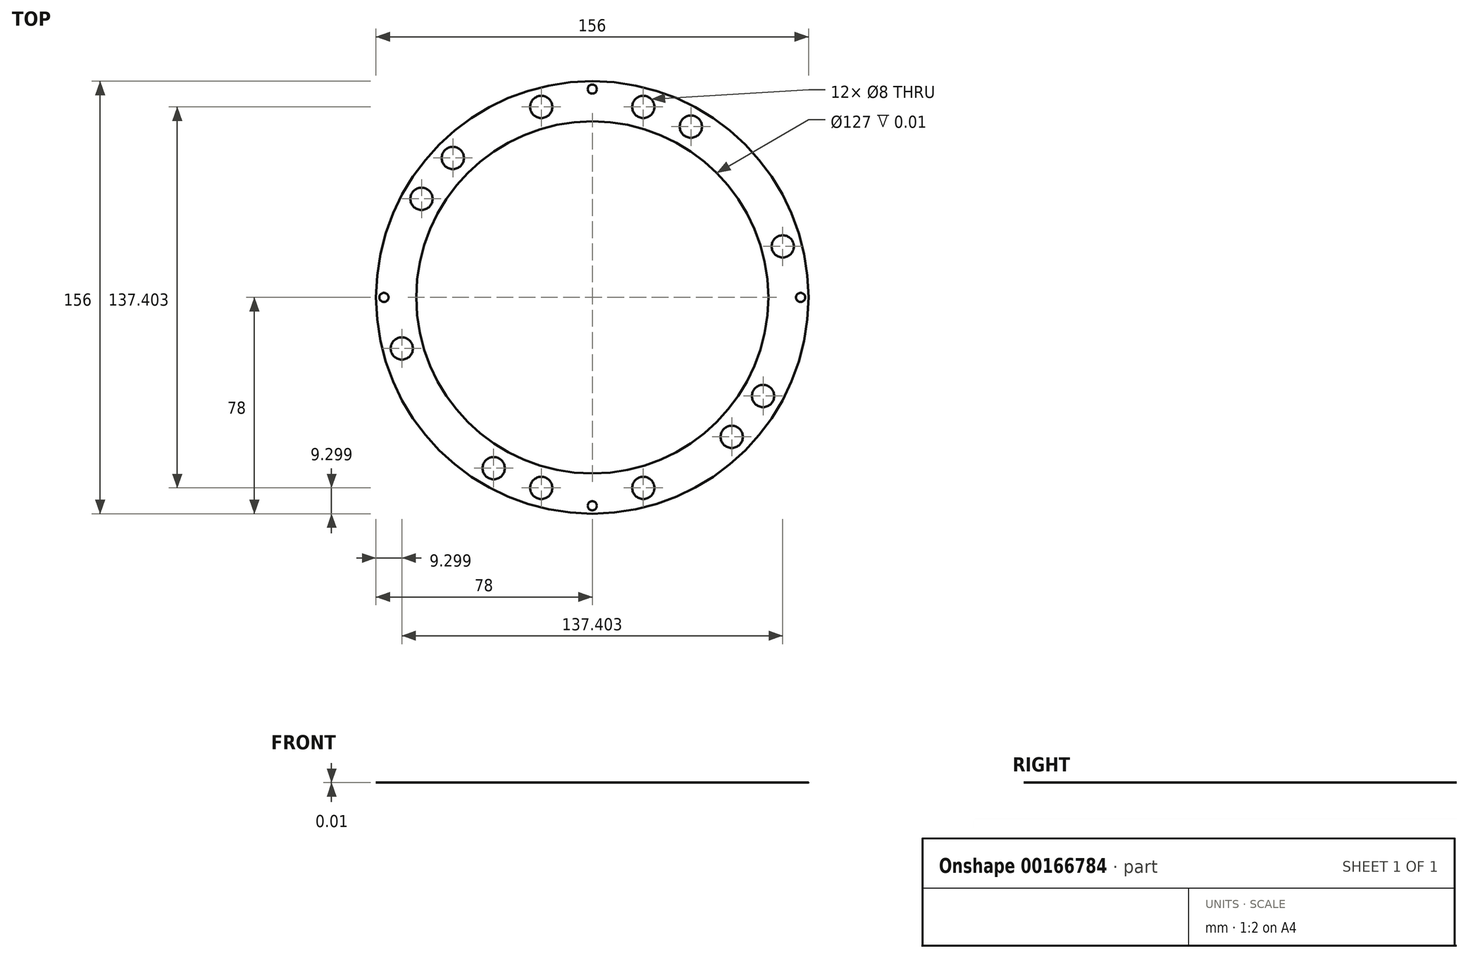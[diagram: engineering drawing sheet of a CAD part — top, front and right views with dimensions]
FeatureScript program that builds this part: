
annotation { "Feature Type Name" : "Feature", "Feature Type Description" : "" }
export const myFeature = defineFeature(function(context is Context, id is Id, definition is map)
    precondition{}
    {
        {
            var Q0;
            Q0=qCreatedBy(makeId("Top.planeOp"),FACE);
            var sketch = newSketch(context, id + "F0", { "sketchPlane" : qUnion([Q0])});
            skCircle(sketch, "E0", {"center": v(0, 0) * mm, "radius": 63.5 * mm});
            skCircle(sketch, "E1", {"center": v(0, 0) * mm, "radius": 78 * mm});
            skCircle(sketch, "E2", {"center": v(75.15, 0) * mm, "radius": 1.65 * mm});
            skCircle(sketch, "E3.1.0", {"center": v(0, 75.15) * mm, "radius": 1.65 * mm});
            skCircle(sketch, "E3.2.0", {"center": v(-75.15, 0) * mm, "radius": 1.65 * mm});
            skCircle(sketch, "E3.3.0", {"center": v(0, -75.15) * mm, "radius": 1.65 * mm});
            skCircle(sketch, "E4", {"center": v(68.7, 18.4) * mm, "radius": 2.38 * mm});
            skCircle(sketch, "E5", {"center": v(35.56, 61.6) * mm, "radius": 2.38 * mm});
            skCircle(sketch, "E6", {"center": v(18.4, 68.7) * mm, "radius": 2.38 * mm});
            skLineSegment(sketch, "E7", {"start": v(68.7, 18.4) * mm, "end": v(0, 0) * mm, "construction": true});
            skLineSegment(sketch, "E8", {"start": v(35.56, 61.6) * mm, "end": v(0, 0) * mm, "construction": true});
            skLineSegment(sketch, "E9", {"start": v(18.4, 68.7) * mm, "end": v(0, 0) * mm, "construction": true});
            skCircle(sketch, "E10.1.0", {"center": v(-18.4, -68.7) * mm, "radius": 2.38 * mm});
            skCircle(sketch, "E10.1.1", {"center": v(-68.7, -18.4) * mm, "radius": 2.38 * mm});
            skCircle(sketch, "E10.1.2", {"center": v(-35.56, -61.6) * mm, "radius": 2.38 * mm});
            skCircle(sketch, "E11", {"center": v(-18.4, 68.7) * mm, "radius": 2.38 * mm});
            skCircle(sketch, "E12", {"center": v(-50.3, 50.3) * mm, "radius": 2.38 * mm});
            skCircle(sketch, "E13", {"center": v(-61.6, 35.56) * mm, "radius": 2.38 * mm});
            skLineSegment(sketch, "E14", {"start": v(0, 0) * mm, "end": v(-18.4, 68.7) * mm, "construction": true});
            skLineSegment(sketch, "E15", {"start": v(0, 0) * mm, "end": v(-50.3, 50.3) * mm, "construction": true});
            skLineSegment(sketch, "E16", {"start": v(0, 0) * mm, "end": v(-61.6, 35.56) * mm, "construction": true});
            skCircle(sketch, "E17.1.0", {"center": v(50.3, -50.3) * mm, "radius": 2.38 * mm});
            skCircle(sketch, "E17.1.1", {"center": v(18.4, -68.7) * mm, "radius": 2.38 * mm});
            skCircle(sketch, "E17.1.2", {"center": v(61.6, -35.56) * mm, "radius": 2.38 * mm});
            skSolve(sketch);
        }
        {
            var Q0;
            Q0=makeQuery(id+"F0.imprint","IMPRINT",FACE,{"disambiguationData":[TD([[makeQuery(id+"F0.imprint","IMPRINT",EDGE,{"derivedFrom":sQuery(id+"F0.wireOp",EDGE,"E0")}),-1.0]])]});
            extrude(context, id + "F1", {"entities" : qUnion([Q0]), "depth" : 1 / 101.6 * mm});
        }
        {
            var Q0;
            Q0=makeQuery(id+"F1.opExtrude","CAP_FACE",FACE,{"disambiguationData":[OSD([sQuery(id+"F0.wireOp",EDGE,"E0"),sQuery(id+"F0.wireOp",EDGE,"E1"),sQuery(id+"F0.wireOp",EDGE,"E2"),sQuery(id+"F0.wireOp",EDGE,"E3.1.0"),sQuery(id+"F0.wireOp",EDGE,"E3.2.0"),sQuery(id+"F0.wireOp",EDGE,"E3.3.0"),sQuery(id+"F0.wireOp",EDGE,"E4"),sQuery(id+"F0.wireOp",EDGE,"E5"),sQuery(id+"F0.wireOp",EDGE,"E6"),sQuery(id+"F0.wireOp",EDGE,"E10.1.0"),sQuery(id+"F0.wireOp",EDGE,"E10.1.1"),sQuery(id+"F0.wireOp",EDGE,"E10.1.2"),sQuery(id+"F0.wireOp",EDGE,"E11"),sQuery(id+"F0.wireOp",EDGE,"E12"),sQuery(id+"F0.wireOp",EDGE,"E13"),sQuery(id+"F0.wireOp",EDGE,"E17.1.0"),sQuery(id+"F0.wireOp",EDGE,"E17.1.1"),sQuery(id+"F0.wireOp",EDGE,"E17.1.2")])],"isStart":false});
            var sketch = newSketch(context, id + "F2", { "sketchPlane" : qUnion([Q0])});
            skCircle(sketch, "E18", {"center": v(68.7, 18.4) * mm, "radius": 4 * mm});
            skCircle(sketch, "E19", {"center": v(35.56, 61.6) * mm, "radius": 4 * mm});
            skCircle(sketch, "E20", {"center": v(18.4, 68.7) * mm, "radius": 4 * mm});
            skCircle(sketch, "E21", {"center": v(-18.4, 68.7) * mm, "radius": 4 * mm});
            skCircle(sketch, "E22", {"center": v(-50.3, 50.3) * mm, "radius": 4 * mm});
            skCircle(sketch, "E23", {"center": v(-61.6, 35.56) * mm, "radius": 4 * mm});
            skCircle(sketch, "E24", {"center": v(-68.7, -18.4) * mm, "radius": 4 * mm});
            skCircle(sketch, "E25", {"center": v(-35.56, -61.6) * mm, "radius": 4 * mm});
            skCircle(sketch, "E26", {"center": v(-18.4, -68.7) * mm, "radius": 4 * mm});
            skCircle(sketch, "E27", {"center": v(18.4, -68.7) * mm, "radius": 4 * mm});
            skCircle(sketch, "E28", {"center": v(50.3, -50.3) * mm, "radius": 4 * mm});
            skCircle(sketch, "E29", {"center": v(61.6, -35.56) * mm, "radius": 4 * mm});
            skSolve(sketch);
        }
        {
            var Q0;
            Q0=qSketchRegion(id+"F2",true);
            extrude(context, id + "F3", {"entities" : qUnion([Q0]), "operationType" : NewBodyOperationType.REMOVE, "oppositeDirection" : true, "depth" : 4 * mm});
        }
    });
